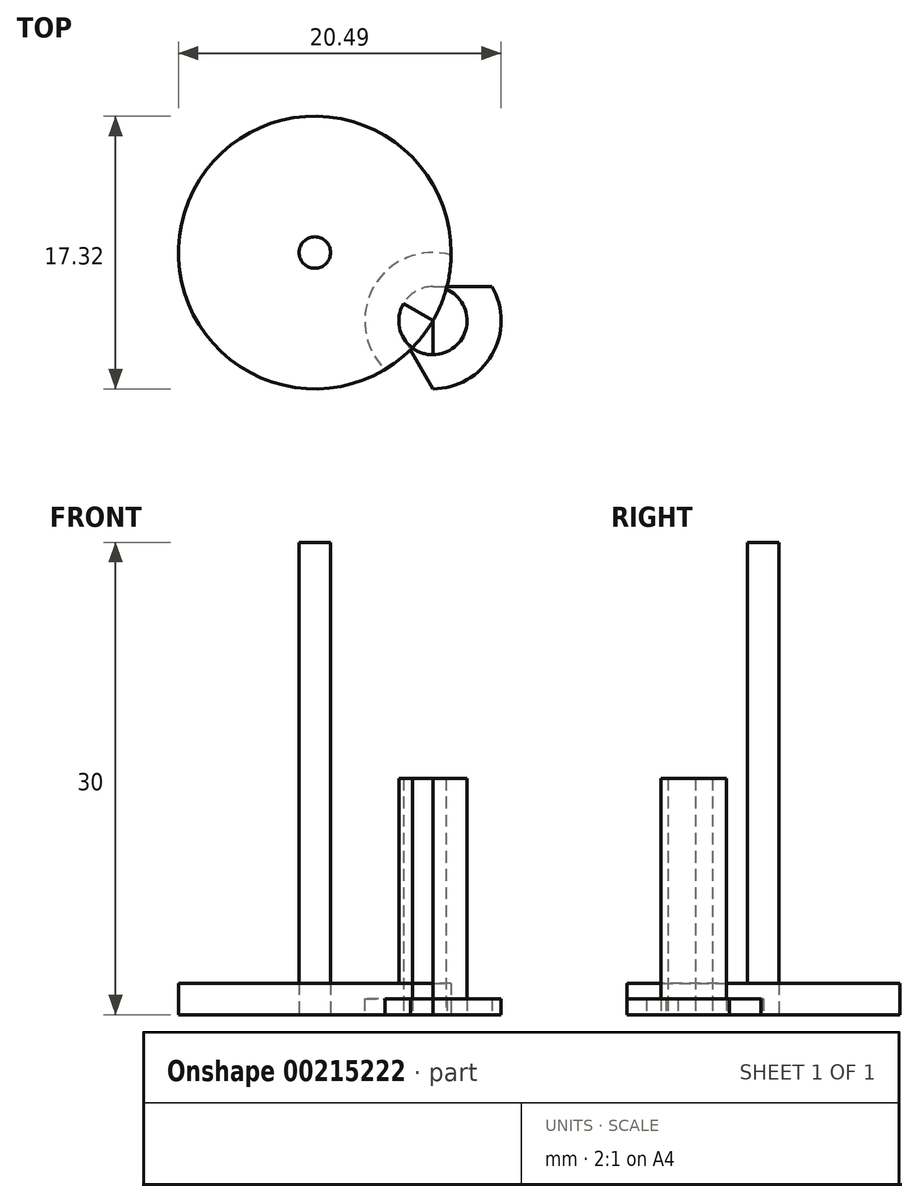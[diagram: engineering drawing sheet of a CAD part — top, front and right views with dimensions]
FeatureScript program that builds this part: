
annotation { "Feature Type Name" : "Feature", "Feature Type Description" : "" }
export const myFeature = defineFeature(function(context is Context, id is Id, definition is map)
    precondition{}
    {
        {
            var Q0;
            Q0=qCreatedBy(makeId("Top.planeOp"),FACE);
            var sketch = newSketch(context, id + "F0", { "sketchPlane" : qUnion([Q0])});
            skLineSegment(sketch, "E0", {"start": v(-7.5, -4.33) * mm, "end": v(7.5, -4.33) * mm});
            skLineSegment(sketch, "E1", {"start": v(7.5, -4.33) * mm, "end": v(0, 8.66) * mm});
            skLineSegment(sketch, "E2", {"start": v(0, 8.66) * mm, "end": v(-7.5, -4.33) * mm});
            skPoint(sketch, "E3.second.point", {"position": v(-3.75, 2.17) * mm});
            skPoint(sketch, "E3.third.point", {"position": v(3.75, 2.17) * mm});
            skCircle(sketch, "E4", {"center": v(0, 0) * mm, "radius": 4.33 * mm});
            skPoint(sketch, "E4.first.point", {"position": v(0, -4.33) * mm});
            skLineSegment(sketch, "E5", {"start": v(0, 0) * mm, "end": v(3.75, 2.17) * mm});
            skLineSegment(sketch, "E6", {"start": v(-3.75, 2.17) * mm, "end": v(0, 0) * mm});
            skLineSegment(sketch, "E7", {"start": v(0, -4.33) * mm, "end": v(0, 0) * mm});
            skCircle(sketch, "E8", {"center": v(0, 8.66) * mm, "radius": 4.33 * mm});
            skCircle(sketch, "E9", {"center": v(-7.5, -4.33) * mm, "radius": 4.33 * mm});
            skCircle(sketch, "E10", {"center": v(7.5, -4.33) * mm, "radius": 4.33 * mm});
            skLineSegment(sketch, "E11", {"start": v(-3.75, 2.17) * mm, "end": v(3.75, 2.17) * mm});
            skLineSegment(sketch, "E12", {"start": v(-3.75, 2.17) * mm, "end": v(0, -4.33) * mm});
            skLineSegment(sketch, "E13", {"start": v(3.75, 2.17) * mm, "end": v(0, -4.33) * mm});
            skCircle(sketch, "E14", {"center": v(0, 0) * mm, "radius": 2.17 * mm});
            skLineSegment(sketch, "E15", {"start": v(-7.5, -4.33) * mm, "end": v(-22.5, -4.33) * mm});
            skLineSegment(sketch, "E16", {"start": v(-22.5, -4.33) * mm, "end": v(-15, 8.66) * mm});
            skLineSegment(sketch, "E17", {"start": v(-15, 8.66) * mm, "end": v(-7.5, -4.33) * mm});
            skLineSegment(sketch, "E18", {"start": v(-15, 8.66) * mm, "end": v(-7.5, 21.65) * mm});
            skLineSegment(sketch, "E19", {"start": v(-7.5, 21.65) * mm, "end": v(0, 8.66) * mm});
            skLineSegment(sketch, "E20", {"start": v(-15, 8.66) * mm, "end": v(0, 8.66) * mm});
            skCircle(sketch, "E21", {"center": v(-7.5, 4.33) * mm, "radius": 8.66 * mm});
            skCircle(sketch, "E22", {"center": v(-7.5, 4.33) * mm, "radius": 1 * mm});
            skSolve(sketch);
        }
        {
            var Q0;
            {var subQ1=sQuery(id+"F0.wireOp",EDGE,"E5");var subQ3=sQuery(id+"F0.wireOp",EDGE,"E14");var subQ4=makeQuery(id+"F0.imprint","INTERSECT",VERTEX,{"derivedFrom":[subQ1,subQ3]});Q0=makeQuery(id+"F0.imprint","IMPRINT",FACE,{"disambiguationData":[TD([[makeQuery(id+"F0.imprint","IMPRINT",EDGE,{"disambiguationData":[TD([[subQ4,-1.0]])],"derivedFrom":subQ3}),1.0]])]});}
            var Q1;
            {var subQ1=sQuery(id+"F0.wireOp",EDGE,"E6");var subQ3=sQuery(id+"F0.wireOp",EDGE,"E14");var subQ4=makeQuery(id+"F0.imprint","INTERSECT",VERTEX,{"derivedFrom":[subQ1,subQ3]});Q1=makeQuery(id+"F0.imprint","IMPRINT",FACE,{"disambiguationData":[TD([[makeQuery(id+"F0.imprint","IMPRINT",EDGE,{"disambiguationData":[TD([[subQ4,-1.0]])],"derivedFrom":subQ3}),1.0]])]});}
            var Q2;
            {var subQ0=sQuery(id+"F0.wireOp",EDGE,"E7");var subQ3=sQuery(id+"F0.wireOp",EDGE,"E14");var subQ5=makeQuery(id+"F0.imprint","INTERSECT",VERTEX,{"derivedFrom":[subQ0,subQ3]});Q2=makeQuery(id+"F0.imprint","IMPRINT",FACE,{"disambiguationData":[TD([[makeQuery(id+"F0.imprint","IMPRINT",EDGE,{"disambiguationData":[TD([[subQ5,-1.0]])],"derivedFrom":subQ3}),1.0]])]});}
            extrude(context, id + "F1", {"entities" : qUnion([Q0, Q1, Q2]), "depth" : 15 * mm});
        }
        {
            var Q0;
            {var subQ1=sQuery(id+"F0.wireOp",EDGE,"E4");var subQ3=makeQuery(id+"F0.imprint","INTERSECT",VERTEX,{"derivedFrom":[subQ1,sQuery(id+"F0.wireOp",EDGE,"E9")]});Q0=makeQuery(id+"F0.imprint","IMPRINT",FACE,{"disambiguationData":[TD([[makeQuery(id+"F0.imprint","IMPRINT",EDGE,{"disambiguationData":[TD([[subQ3,1.0]])],"derivedFrom":subQ1}),1.0]])]});}
            var Q1;
            {var subQ1=sQuery(id+"F0.wireOp",EDGE,"E6");var subQ3=sQuery(id+"F0.wireOp",EDGE,"E14");var subQ4=makeQuery(id+"F0.imprint","INTERSECT",VERTEX,{"derivedFrom":[subQ1,subQ3]});Q1=makeQuery(id+"F0.imprint","IMPRINT",FACE,{"disambiguationData":[TD([[makeQuery(id+"F0.imprint","IMPRINT",EDGE,{"disambiguationData":[TD([[subQ4,-1.0]])],"derivedFrom":subQ3}),-1.0]])]});}
            var Q2;
            {var subQ1=sQuery(id+"F0.wireOp",EDGE,"E6");var subQ3=sQuery(id+"F0.wireOp",EDGE,"E14");var subQ4=makeQuery(id+"F0.imprint","INTERSECT",VERTEX,{"derivedFrom":[subQ1,subQ3]});Q2=makeQuery(id+"F0.imprint","IMPRINT",FACE,{"disambiguationData":[TD([[makeQuery(id+"F0.imprint","IMPRINT",EDGE,{"disambiguationData":[TD([[subQ4,1.0]])],"derivedFrom":subQ3}),-1.0]])]});}
            var Q3;
            {var subQ1=sQuery(id+"F0.wireOp",EDGE,"E4");var subQ3=makeQuery(id+"F0.imprint","INTERSECT",VERTEX,{"derivedFrom":[subQ1,sQuery(id+"F0.wireOp",EDGE,"E8")]});Q3=makeQuery(id+"F0.imprint","IMPRINT",FACE,{"disambiguationData":[TD([[makeQuery(id+"F0.imprint","IMPRINT",EDGE,{"disambiguationData":[TD([[subQ3,1.0]])],"derivedFrom":subQ1}),1.0]])]});}
            var Q4;
            {var subQ1=sQuery(id+"F0.wireOp",EDGE,"E5");var subQ3=sQuery(id+"F0.wireOp",EDGE,"E14");var subQ4=makeQuery(id+"F0.imprint","INTERSECT",VERTEX,{"derivedFrom":[subQ1,subQ3]});Q4=makeQuery(id+"F0.imprint","IMPRINT",FACE,{"disambiguationData":[TD([[makeQuery(id+"F0.imprint","IMPRINT",EDGE,{"disambiguationData":[TD([[subQ4,-1.0]])],"derivedFrom":subQ3}),-1.0]])]});}
            var Q5;
            {var subQ1=sQuery(id+"F0.wireOp",EDGE,"E5");var subQ3=sQuery(id+"F0.wireOp",EDGE,"E14");var subQ4=makeQuery(id+"F0.imprint","INTERSECT",VERTEX,{"derivedFrom":[subQ1,subQ3]});Q5=makeQuery(id+"F0.imprint","IMPRINT",FACE,{"disambiguationData":[TD([[makeQuery(id+"F0.imprint","IMPRINT",EDGE,{"disambiguationData":[TD([[subQ4,1.0]])],"derivedFrom":subQ3}),-1.0]])]});}
            var Q6;
            {var subQ1=sQuery(id+"F0.wireOp",EDGE,"E4");var subQ3=makeQuery(id+"F0.imprint","INTERSECT",VERTEX,{"derivedFrom":[subQ1,sQuery(id+"F0.wireOp",EDGE,"E10")]});Q6=makeQuery(id+"F0.imprint","IMPRINT",FACE,{"disambiguationData":[TD([[makeQuery(id+"F0.imprint","IMPRINT",EDGE,{"disambiguationData":[TD([[subQ3,1.0]])],"derivedFrom":subQ1}),1.0]])]});}
            var Q7;
            {var subQ1=sQuery(id+"F0.wireOp",EDGE,"E7");var subQ3=sQuery(id+"F0.wireOp",EDGE,"E14");var subQ4=makeQuery(id+"F0.imprint","INTERSECT",VERTEX,{"derivedFrom":[subQ1,subQ3]});Q7=makeQuery(id+"F0.imprint","IMPRINT",FACE,{"disambiguationData":[TD([[makeQuery(id+"F0.imprint","IMPRINT",EDGE,{"disambiguationData":[TD([[subQ4,-1.0]])],"derivedFrom":subQ3}),-1.0]])]});}
            var Q8;
            {var subQ1=sQuery(id+"F0.wireOp",EDGE,"E7");var subQ3=sQuery(id+"F0.wireOp",EDGE,"E14");var subQ4=makeQuery(id+"F0.imprint","INTERSECT",VERTEX,{"derivedFrom":[subQ1,subQ3]});Q8=makeQuery(id+"F0.imprint","IMPRINT",FACE,{"disambiguationData":[TD([[makeQuery(id+"F0.imprint","IMPRINT",EDGE,{"disambiguationData":[TD([[subQ4,1.0]])],"derivedFrom":subQ3}),-1.0]])]});}
            var Q9;
            {var subQ1=sQuery(id+"F0.wireOp",EDGE,"E6");var subQ3=sQuery(id+"F0.wireOp",EDGE,"E14");var subQ4=makeQuery(id+"F0.imprint","INTERSECT",VERTEX,{"derivedFrom":[subQ1,subQ3]});Q9=makeQuery(id+"F0.imprint","IMPRINT",FACE,{"disambiguationData":[TD([[makeQuery(id+"F0.imprint","IMPRINT",EDGE,{"disambiguationData":[TD([[subQ4,-1.0]])],"derivedFrom":subQ3}),1.0]])]});}
            var Q10;
            {var subQ0=sQuery(id+"F0.wireOp",EDGE,"E7");var subQ3=sQuery(id+"F0.wireOp",EDGE,"E14");var subQ5=makeQuery(id+"F0.imprint","INTERSECT",VERTEX,{"derivedFrom":[subQ0,subQ3]});Q10=makeQuery(id+"F0.imprint","IMPRINT",FACE,{"disambiguationData":[TD([[makeQuery(id+"F0.imprint","IMPRINT",EDGE,{"disambiguationData":[TD([[subQ5,-1.0]])],"derivedFrom":subQ3}),1.0]])]});}
            var Q11;
            {var subQ1=sQuery(id+"F0.wireOp",EDGE,"E5");var subQ3=sQuery(id+"F0.wireOp",EDGE,"E14");var subQ4=makeQuery(id+"F0.imprint","INTERSECT",VERTEX,{"derivedFrom":[subQ1,subQ3]});Q11=makeQuery(id+"F0.imprint","IMPRINT",FACE,{"disambiguationData":[TD([[makeQuery(id+"F0.imprint","IMPRINT",EDGE,{"disambiguationData":[TD([[subQ4,-1.0]])],"derivedFrom":subQ3}),1.0]])]});}
            extrude(context, id + "F2", {"entities" : qUnion([Q0, Q1, Q2, Q3, Q4, Q5, Q6, Q7, Q8, Q9, Q10, Q11]), "depth" : 1 * mm});
        }
        {
            var Q0;
            {var subQ0=sQuery(id+"F0.wireOp",EDGE,"E17");var subQ1=sQuery(id+"F0.wireOp",EDGE,"E9");var subQ2=makeQuery(id+"F0.imprint","INTERSECT",VERTEX,{"derivedFrom":[subQ1,subQ0]});Q0=makeQuery(id+"F0.imprint","IMPRINT",FACE,{"disambiguationData":[TD([[makeQuery(id+"F0.imprint","IMPRINT",EDGE,{"disambiguationData":[TD([[subQ2,-1.0]])],"derivedFrom":subQ1}),-1.0]])]});}
            var Q1;
            Q1=makeQuery(id+"F0.imprint","IMPRINT",FACE,{"disambiguationData":[TD([[makeQuery(id+"F0.imprint","IMPRINT",EDGE,{"derivedFrom":sQuery(id+"F0.wireOp",EDGE,"E22")}),-1.0]])]});
            var Q2;
            {var subQ0=sQuery(id+"F0.wireOp",EDGE,"E21");var subQ1=sQuery(id+"F0.wireOp",EDGE,"E8");var subQ2=makeQuery(id+"F0.imprint","INTERSECT",VERTEX,{"disambiguationData":[OD(0.0)],"derivedFrom":[subQ1,subQ0]});Q2=makeQuery(id+"F0.imprint","IMPRINT",FACE,{"disambiguationData":[TD([[makeQuery(id+"F0.imprint","IMPRINT",EDGE,{"disambiguationData":[TD([[subQ2,-1.0]])],"derivedFrom":subQ1}),-1.0]])]});}
            var Q3;
            {var subQ0=sQuery(id+"F0.wireOp",EDGE,"E21");var subQ1=sQuery(id+"F0.wireOp",EDGE,"E8");var subQ2=makeQuery(id+"F0.imprint","INTERSECT",VERTEX,{"disambiguationData":[OD(0.0)],"derivedFrom":[subQ1,subQ0]});Q3=makeQuery(id+"F0.imprint","IMPRINT",FACE,{"disambiguationData":[TD([[makeQuery(id+"F0.imprint","IMPRINT",EDGE,{"disambiguationData":[TD([[subQ2,-1.0]])],"derivedFrom":subQ1}),1.0]])]});}
            var Q4;
            {var subQ1=sQuery(id+"F0.wireOp",EDGE,"E2");var subQ3=sQuery(id+"F0.wireOp",EDGE,"E8");var subQ4=makeQuery(id+"F0.imprint","INTERSECT",VERTEX,{"derivedFrom":[subQ1,subQ3]});Q4=makeQuery(id+"F0.imprint","IMPRINT",FACE,{"disambiguationData":[TD([[makeQuery(id+"F0.imprint","IMPRINT",EDGE,{"disambiguationData":[TD([[subQ4,1.0]])],"derivedFrom":subQ3}),1.0]])]});}
            var Q5;
            {var subQ1=sQuery(id+"F0.wireOp",EDGE,"E2");var subQ3=sQuery(id+"F0.wireOp",EDGE,"E8");var subQ4=makeQuery(id+"F0.imprint","INTERSECT",VERTEX,{"derivedFrom":[subQ1,subQ3]});Q5=makeQuery(id+"F0.imprint","IMPRINT",FACE,{"disambiguationData":[TD([[makeQuery(id+"F0.imprint","IMPRINT",EDGE,{"disambiguationData":[TD([[subQ4,-1.0]])],"derivedFrom":subQ3}),1.0]])]});}
            var Q6;
            {var subQ1=sQuery(id+"F0.wireOp",EDGE,"E2");var subQ3=sQuery(id+"F0.wireOp",EDGE,"E8");var subQ4=makeQuery(id+"F0.imprint","INTERSECT",VERTEX,{"derivedFrom":[subQ1,subQ3]});Q6=makeQuery(id+"F0.imprint","IMPRINT",FACE,{"disambiguationData":[TD([[makeQuery(id+"F0.imprint","IMPRINT",EDGE,{"disambiguationData":[TD([[subQ4,-1.0]])],"derivedFrom":subQ3}),-1.0]])]});}
            var Q7;
            {var subQ2=sQuery(id+"F0.wireOp",EDGE,"E21");var subQ4=sQuery(id+"F0.wireOp",EDGE,"E4");var subQ5=makeQuery(id+"F0.imprint","INTERSECT",VERTEX,{"disambiguationData":[OD(0.0)],"derivedFrom":[subQ4,subQ2]});Q7=makeQuery(id+"F0.imprint","IMPRINT",FACE,{"disambiguationData":[TD([[makeQuery(id+"F0.imprint","IMPRINT",EDGE,{"disambiguationData":[TD([[subQ5,-1.0]])],"derivedFrom":subQ4}),1.0]])]});}
            var Q8;
            {var subQ1=sQuery(id+"F0.wireOp",EDGE,"E6");var subQ3=sQuery(id+"F0.wireOp",EDGE,"E14");var subQ4=makeQuery(id+"F0.imprint","INTERSECT",VERTEX,{"derivedFrom":[subQ1,subQ3]});Q8=makeQuery(id+"F0.imprint","IMPRINT",FACE,{"disambiguationData":[TD([[makeQuery(id+"F0.imprint","IMPRINT",EDGE,{"disambiguationData":[TD([[subQ4,1.0]])],"derivedFrom":subQ3}),-1.0]])]});}
            var Q9;
            {var subQ1=sQuery(id+"F0.wireOp",EDGE,"E6");var subQ3=sQuery(id+"F0.wireOp",EDGE,"E14");var subQ4=makeQuery(id+"F0.imprint","INTERSECT",VERTEX,{"derivedFrom":[subQ1,subQ3]});Q9=makeQuery(id+"F0.imprint","IMPRINT",FACE,{"disambiguationData":[TD([[makeQuery(id+"F0.imprint","IMPRINT",EDGE,{"disambiguationData":[TD([[subQ4,-1.0]])],"derivedFrom":subQ3}),-1.0]])]});}
            var Q10;
            {var subQ1=sQuery(id+"F0.wireOp",EDGE,"E2");var subQ3=sQuery(id+"F0.wireOp",EDGE,"E9");var subQ4=makeQuery(id+"F0.imprint","INTERSECT",VERTEX,{"derivedFrom":[subQ1,subQ3]});Q10=makeQuery(id+"F0.imprint","IMPRINT",FACE,{"disambiguationData":[TD([[makeQuery(id+"F0.imprint","IMPRINT",EDGE,{"disambiguationData":[TD([[subQ4,1.0]])],"derivedFrom":subQ3}),-1.0]])]});}
            var Q11;
            {var subQ4=sQuery(id+"F0.wireOp",EDGE,"E4");var subQ6=makeQuery(id+"F0.imprint","INTERSECT",VERTEX,{"derivedFrom":[subQ4,sQuery(id+"F0.wireOp",EDGE,"E9")]});Q11=makeQuery(id+"F0.imprint","IMPRINT",FACE,{"disambiguationData":[TD([[makeQuery(id+"F0.imprint","IMPRINT",EDGE,{"disambiguationData":[TD([[subQ6,-1.0]])],"derivedFrom":subQ4}),1.0]])]});}
            var Q12;
            {var subQ3=sQuery(id+"F0.wireOp",EDGE,"E9");var subQ5=makeQuery(id+"F0.imprint","INTERSECT",VERTEX,{"derivedFrom":[sQuery(id+"F0.wireOp",EDGE,"E4"),subQ3]});Q12=makeQuery(id+"F0.imprint","IMPRINT",FACE,{"disambiguationData":[TD([[makeQuery(id+"F0.imprint","IMPRINT",EDGE,{"disambiguationData":[TD([[subQ5,1.0]])],"derivedFrom":subQ3}),1.0]])]});}
            var Q13;
            {var subQ1=sQuery(id+"F0.wireOp",EDGE,"E2");var subQ3=sQuery(id+"F0.wireOp",EDGE,"E9");var subQ4=makeQuery(id+"F0.imprint","INTERSECT",VERTEX,{"derivedFrom":[subQ1,subQ3]});Q13=makeQuery(id+"F0.imprint","IMPRINT",FACE,{"disambiguationData":[TD([[makeQuery(id+"F0.imprint","IMPRINT",EDGE,{"disambiguationData":[TD([[subQ4,-1.0]])],"derivedFrom":subQ3}),1.0]])]});}
            var Q14;
            {var subQ0=sQuery(id+"F0.wireOp",EDGE,"E17");var subQ1=sQuery(id+"F0.wireOp",EDGE,"E9");var subQ2=makeQuery(id+"F0.imprint","INTERSECT",VERTEX,{"derivedFrom":[subQ1,subQ0]});Q14=makeQuery(id+"F0.imprint","IMPRINT",FACE,{"disambiguationData":[TD([[makeQuery(id+"F0.imprint","IMPRINT",EDGE,{"disambiguationData":[TD([[subQ2,-1.0]])],"derivedFrom":subQ1}),1.0]])]});}
            var Q15;
            {var subQ0=sQuery(id+"F0.wireOp",EDGE,"E21");var subQ1=sQuery(id+"F0.wireOp",EDGE,"E4");var subQ2=makeQuery(id+"F0.imprint","INTERSECT",VERTEX,{"disambiguationData":[OD(0.0)],"derivedFrom":[subQ1,subQ0]});Q15=makeQuery(id+"F0.imprint","IMPRINT",FACE,{"disambiguationData":[TD([[makeQuery(id+"F0.imprint","IMPRINT",EDGE,{"disambiguationData":[TD([[subQ2,-1.0]])],"derivedFrom":subQ1}),-1.0]])]});}
            var Q16;
            {var subQ3=sQuery(id+"F0.wireOp",EDGE,"E14");var subQ5=makeQuery(id+"F0.imprint","INTERSECT",VERTEX,{"derivedFrom":[sQuery(id+"F0.wireOp",EDGE,"E11"),subQ3]});Q16=makeQuery(id+"F0.imprint","IMPRINT",FACE,{"disambiguationData":[TD([[makeQuery(id+"F0.imprint","IMPRINT",EDGE,{"disambiguationData":[TD([[subQ5,1.0]])],"derivedFrom":subQ3}),1.0]])]});}
            var Q17;
            {var subQ0=sQuery(id+"F0.wireOp",EDGE,"E14");var subQ1=sQuery(id+"F0.wireOp",EDGE,"E11");var subQ2=makeQuery(id+"F0.imprint","INTERSECT",VERTEX,{"derivedFrom":[subQ1,subQ0]});Q17=makeQuery(id+"F0.imprint","IMPRINT",FACE,{"disambiguationData":[TD([[makeQuery(id+"F0.imprint","IMPRINT",EDGE,{"disambiguationData":[TD([[subQ2,-1.0]])],"derivedFrom":subQ1}),-1.0]])]});}
            var Q18;
            {var subQ1=sQuery(id+"F0.wireOp",EDGE,"E6");var subQ3=sQuery(id+"F0.wireOp",EDGE,"E14");var subQ4=makeQuery(id+"F0.imprint","INTERSECT",VERTEX,{"derivedFrom":[subQ1,subQ3]});Q18=makeQuery(id+"F0.imprint","IMPRINT",FACE,{"disambiguationData":[TD([[makeQuery(id+"F0.imprint","IMPRINT",EDGE,{"disambiguationData":[TD([[subQ4,-1.0]])],"derivedFrom":subQ3}),1.0]])]});}
            var Q19;
            {var subQ0=sQuery(id+"F0.wireOp",EDGE,"E9");var subQ1=sQuery(id+"F0.wireOp",EDGE,"E4");var subQ2=makeQuery(id+"F0.imprint","INTERSECT",VERTEX,{"derivedFrom":[subQ1,subQ0]});Q19=makeQuery(id+"F0.imprint","IMPRINT",FACE,{"disambiguationData":[TD([[makeQuery(id+"F0.imprint","IMPRINT",EDGE,{"disambiguationData":[TD([[subQ2,-1.0]])],"derivedFrom":subQ1}),-1.0]])]});}
            var Q20;
            {var subQ0=sQuery(id+"F0.wireOp",EDGE,"E14");var subQ1=sQuery(id+"F0.wireOp",EDGE,"E12");var subQ2=makeQuery(id+"F0.imprint","INTERSECT",VERTEX,{"derivedFrom":[subQ1,subQ0]});Q20=makeQuery(id+"F0.imprint","IMPRINT",FACE,{"disambiguationData":[TD([[makeQuery(id+"F0.imprint","IMPRINT",EDGE,{"disambiguationData":[TD([[subQ2,-1.0]])],"derivedFrom":subQ1}),1.0]])]});}
            var Q21;
            Q21=makeQuery(id+"F0.imprint","IMPRINT",FACE,{"disambiguationData":[TD([[makeQuery(id+"F0.imprint","IMPRINT",EDGE,{"derivedFrom":sQuery(id+"F0.wireOp",EDGE,"E22")}),1.0]])]});
            extrude(context, id + "F3", {"entities" : qUnion([Q0, Q1, Q2, Q3, Q4, Q5, Q6, Q7, Q8, Q9, Q10, Q11, Q12, Q13, Q14, Q15, Q16, Q17, Q18, Q19, Q20, Q21]), "depth" : 2 * mm});
        }
        {
            var Q0;
            Q0=makeQuery(id+"F0.imprint","IMPRINT",FACE,{"disambiguationData":[TD([[makeQuery(id+"F0.imprint","IMPRINT",EDGE,{"derivedFrom":sQuery(id+"F0.wireOp",EDGE,"E22")}),1.0]])]});
            extrude(context, id + "F4", {"entities" : qUnion([Q0]), "depth" : 30 * mm});
        }
    });
